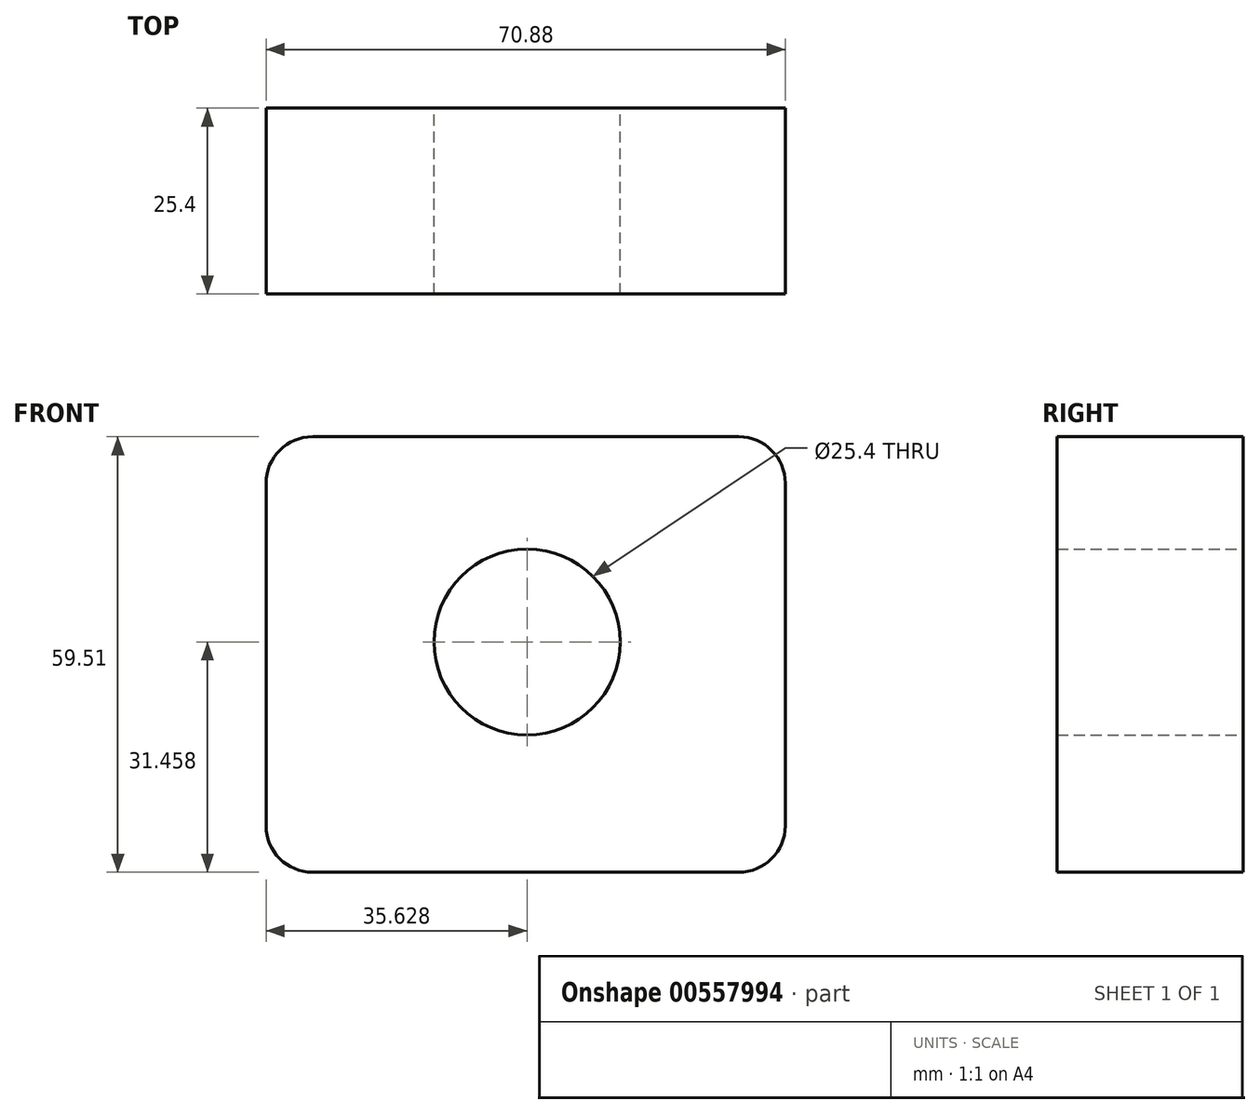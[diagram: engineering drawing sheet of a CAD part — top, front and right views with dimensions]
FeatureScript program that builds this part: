
annotation { "Feature Type Name" : "Feature", "Feature Type Description" : "" }
export const myFeature = defineFeature(function(context is Context, id is Id, definition is map)
    precondition{}
    {
        {
            var Q0;
            Q0=qCreatedBy(makeId("Front.planeOp"),FACE);
            var sketch = newSketch(context, id + "F0", { "sketchPlane" : qUnion([Q0])});
            skLineSegment(sketch, "E0.bottom", {"start": v(6.35, 0) * mm, "end": v(64.53, 0) * mm});
            skLineSegment(sketch, "E0.top", {"start": v(6.35, 59.5) * mm, "end": v(64.53, 59.5) * mm});
            skLineSegment(sketch, "E0.left", {"start": v(0, 6.35) * mm, "end": v(0, 53.16) * mm});
            skLineSegment(sketch, "E0.right", {"start": v(70.88, 6.35) * mm, "end": v(70.88, 53.16) * mm});
            skPoint(sketch, "E1.visualSharp", {"position": v(70.88, 59.5) * mm});
            skArc(sketch, "E1.filletArc", {"start": v(70.88, 53.16) * mm, "mid": v(69.02, 57.65) * mm, "end": v(64.53, 59.5) * mm});
            skPoint(sketch, "E2.visualSharp", {"position": v(0, 59.5) * mm});
            skArc(sketch, "E2.filletArc", {"start": v(6.35, 59.5) * mm, "mid": v(1.86, 57.65) * mm, "end": v(0, 53.16) * mm});
            skPoint(sketch, "E3.visualSharp", {"position": v(0, 0) * mm});
            skArc(sketch, "E3.filletArc", {"start": v(0, 6.35) * mm, "mid": v(1.86, 1.86) * mm, "end": v(6.35, 0) * mm});
            skPoint(sketch, "E4.visualSharp", {"position": v(70.88, 0) * mm});
            skArc(sketch, "E4.filletArc", {"start": v(64.53, 0) * mm, "mid": v(69.02, 1.86) * mm, "end": v(70.88, 6.35) * mm});
            skCircle(sketch, "E5", {"center": v(35.63, 31.46) * mm, "radius": 12.7 * mm});
            skSolve(sketch);
        }
        {
            var Q0;
            Q0=makeQuery(id+"F0.imprint","IMPRINT",FACE,{"disambiguationData":[TD([[makeQuery(id+"F0.imprint","IMPRINT",EDGE,{"derivedFrom":sQuery(id+"F0.wireOp",EDGE,"E0.bottom")}),1.0]])]});
            extrude(context, id + "F1", {"entities" : qUnion([Q0]), "endBound" : BoundingType.SYMMETRIC, "depth" : 25.4 * mm, "offsetDistance" : 25.4 * mm});
        }
    });
